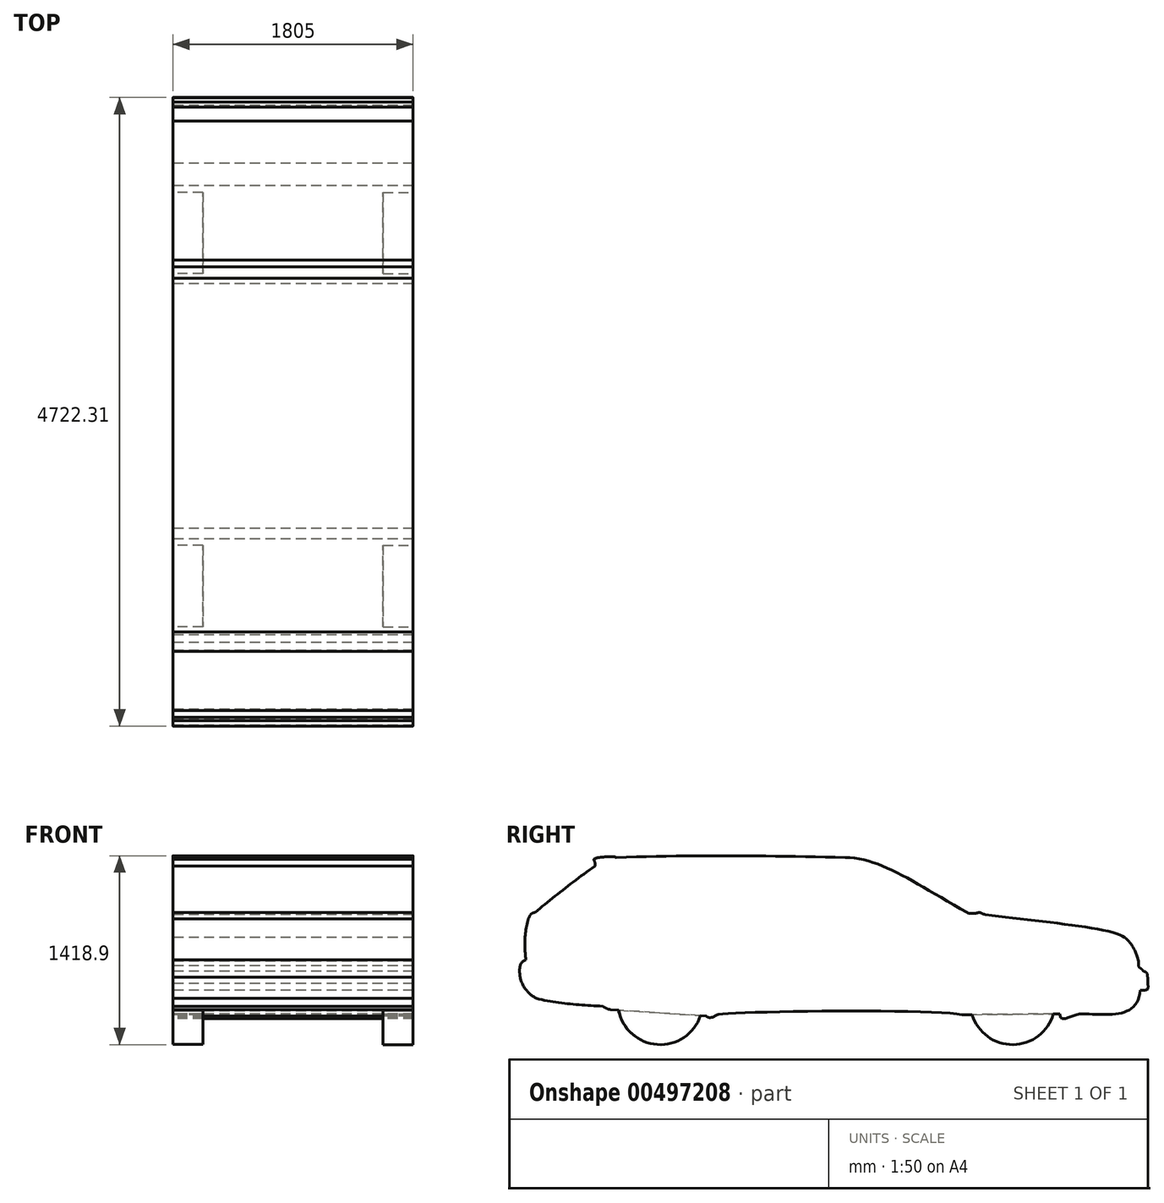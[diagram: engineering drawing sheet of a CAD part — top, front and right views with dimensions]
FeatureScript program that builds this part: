
annotation { "Feature Type Name" : "Feature", "Feature Type Description" : "" }
export const myFeature = defineFeature(function(context is Context, id is Id, definition is map)
    precondition{}
    {
        {
            var Q0;
            Q0=qCreatedBy(makeId("Right.planeOp"),FACE);
            var sketch = newSketch(context, id + "F0", { "sketchPlane" : qUnion([Q0])});
            skFitSpline(sketch, "E0", {"points": [v(1014.45, 1014.59) * mm, v(98.52, 1428.8) * mm], "startDerivative": vector(-1208.9, 676.68) * mm, "endDerivative": vector(-805.93, 15.2) * mm});
            skFitSpline(sketch, "E1", {"points": [v(98.52, 1428.8) * mm, v(-1621.84, 1428.8) * mm], "startDerivative": vector(-1726.02, 42.39) * mm, "endDerivative": vector(-1726.24, -56.33) * mm});
            skFitSpline(sketch, "E2", {"points": [v(-1621.84, 1428.8) * mm, v(-1641.32, 1434.74) * mm], "startDerivative": vector(-28.04, -1.19) * mm, "endDerivative": vector(-37.07, 0.95) * mm});
            skFitSpline(sketch, "E3", {"points": [v(-1641.32, 1434.74) * mm, v(-1789.27, 1416.05) * mm], "startDerivative": vector(-186.28, 7.6) * mm, "endDerivative": vector(-4.75, -28.51) * mm});
            skFitSpline(sketch, "E4", {"points": [v(-1789.27, 1416.05) * mm, v(-1782.87, 1389.44) * mm], "startDerivative": vector(-3.8, -40.87) * mm, "endDerivative": vector(7.6, -42.77) * mm});
            skFitSpline(sketch, "E5", {"points": [v(-1782.87, 1389.44) * mm, v(-1782.87, 1364.14) * mm], "startDerivative": vector(4.26, -24.24) * mm, "endDerivative": vector(-10.86, -12.24) * mm});
            skFitSpline(sketch, "E6", {"points": [v(-1782.87, 1364.14) * mm, v(-2232.94, 1015.64) * mm], "startDerivative": vector(-478.61, -337.99) * mm, "endDerivative": vector(-426.28, -348.1) * mm});
            skFitSpline(sketch, "E7", {"points": [v(-2232.94, 1015.64) * mm, v(-2282.57, 967.54) * mm], "startDerivative": vector(-103.2, -19.3) * mm, "endDerivative": vector(-40.32, -90.05) * mm});
            skFitSpline(sketch, "E8", {"points": [v(-2282.57, 967.54) * mm, v(-2301.84, 658.4) * mm], "startDerivative": vector(-98.12, -310.48) * mm, "endDerivative": vector(29.57, -294.35) * mm});
            skFitSpline(sketch, "E9", {"points": [v(-2301.84, 658.4) * mm, v(-2344.4, 529.38) * mm], "startDerivative": vector(-163.97, -44.35) * mm, "endDerivative": vector(22.85, -147.85) * mm});
            skFitSpline(sketch, "E10", {"points": [v(-2344.4, 529.38) * mm, v(-2222.54, 368.99) * mm], "startDerivative": vector(49.73, -247.3) * mm, "endDerivative": vector(158.6, -94.08) * mm});
            skFitSpline(sketch, "E11", {"points": [v(-2222.54, 368.99) * mm, v(-1723, 310.74) * mm], "startDerivative": vector(462.35, -111.56) * mm, "endDerivative": vector(508.05, -28.23) * mm});
            skFitSpline(sketch, "E12", {"points": [v(-1723, 310.74) * mm, v(-1637.88, 306.71) * mm], "startDerivative": vector(77.96, -63.17) * mm, "endDerivative": vector(4.03, 115.59) * mm});
            skFitSpline(sketch, "E13", {"points": [v(-1637.88, 306.71) * mm, v(-1412.97, 702.76) * mm], "startDerivative": vector(-33.6, 659.93) * mm, "endDerivative": vector(388.43, 166.66) * mm});
            skFitSpline(sketch, "E14", {"points": [v(-1412.97, 702.76) * mm, v(-989.15, 553.57) * mm], "startDerivative": vector(462.35, 104.84) * mm, "endDerivative": vector(279.56, -498.64) * mm});
            skFitSpline(sketch, "E15", {"points": [v(-989.15, 553.57) * mm, v(-944.22, 237) * mm], "startDerivative": vector(157.63, -296.38) * mm, "endDerivative": vector(-8.06, -315.85) * mm});
            skFitSpline(sketch, "E16", {"points": [v(-944.22, 237) * mm, v(-865.37, 246.45) * mm], "startDerivative": vector(2.69, -26.88) * mm, "endDerivative": vector(133.06, 102.15) * mm});
            skFitSpline(sketch, "E17", {"points": [v(-865.37, 246.45) * mm, v(973.8, 246.45) * mm], "startDerivative": vector(92.89, 73.19) * mm, "endDerivative": vector(693.53, -148.45) * mm});
            skFitSpline(sketch, "E18", {"points": [v(973.8, 246.45) * mm, v(1331.5, 736.23) * mm], "startDerivative": vector(26.53, 662.38) * mm, "endDerivative": vector(897.39, 74.6) * mm});
            skFitSpline(sketch, "E19", {"points": [v(1331.5, 736.23) * mm, v(1709.74, 254) * mm], "startDerivative": vector(691.69, 18.08) * mm, "endDerivative": vector(-90.42, -870.26) * mm});
            skFitSpline(sketch, "E20", {"points": [v(1709.74, 254) * mm, v(1880.03, 254) * mm], "startDerivative": vector(15.82, -241.86) * mm, "endDerivative": vector(259.95, 13.56) * mm});
            skFitSpline(sketch, "E21", {"points": [v(1880.03, 254) * mm, v(2315.53, 431.07) * mm], "startDerivative": vector(580.93, -15.82) * mm, "endDerivative": vector(63.3, 660.04) * mm});
            skFitSpline(sketch, "E22", {"points": [v(2315.53, 431.07) * mm, v(2372.04, 482.3) * mm], "startDerivative": vector(180.83, 0) * mm, "endDerivative": vector(-11.3, 153.7) * mm});
            skFitSpline(sketch, "E23", {"points": [v(2372.04, 482.3) * mm, v(2338.14, 574.99) * mm], "startDerivative": vector(-13.56, 223.78) * mm, "endDerivative": vector(-115.28, 36.17) * mm});
            skFitSpline(sketch, "E24", {"points": [v(2338.14, 574.99) * mm, v(2301.22, 614.92) * mm], "startDerivative": vector(-38.43, 70.07) * mm, "endDerivative": vector(-40.69, 83.64) * mm});
            skFitSpline(sketch, "E25", {"points": [v(2301.22, 614.92) * mm, v(2301.22, 649.58) * mm], "startDerivative": vector(0, 34.66) * mm, "endDerivative": vector(0, 34.66) * mm});
            skFitSpline(sketch, "E26", {"points": [v(2301.22, 649.58) * mm, v(2198, 827.4) * mm], "startDerivative": vector(-72.33, 250.9) * mm, "endDerivative": vector(-169.53, 144.67) * mm});
            skFitSpline(sketch, "E27", {"points": [v(2198, 827.4) * mm, v(1151.42, 999.95) * mm], "startDerivative": vector(-291.6, 235.08) * mm, "endDerivative": vector(-1082.74, 153.7) * mm});
            skFitSpline(sketch, "E28", {"points": [v(1151.42, 999.95) * mm, v(1101.48, 1014.96) * mm], "startDerivative": vector(-72.96, 5.5) * mm, "endDerivative": vector(-65.55, 0) * mm});
            skFitSpline(sketch, "E29", {"points": [v(1101.48, 1014.96) * mm, v(1014.45, 1014.59) * mm], "startDerivative": vector(-97.2, -27.13) * mm, "endDerivative": vector(-49.59, 34.86) * mm});
            skLineSegment(sketch, "E30", {"start": v(1709.74, 254) * mm, "end": v(973.8, 246.45) * mm});
            skLineSegment(sketch, "E31", {"start": v(-944.22, 237) * mm, "end": v(-1663.57, 285.48) * mm});
            skSolve(sketch);
        }
        {
            var Q0;
            Q0=makeQuery(id+"F0.imprint","IMPRINT",FACE,{"disambiguationData":[TD([[makeQuery(id+"F0.imprint","IMPRINT",EDGE,{"derivedFrom":sQuery(id+"F0.wireOp",EDGE,"E0")}),1.0]])]});
            var Q1;
            Q1=makeQuery(id+"F0.imprint","IMPRINT",FACE,{"disambiguationData":[TD([[makeQuery(id+"F0.imprint","IMPRINT",EDGE,{"derivedFrom":sQuery(id+"F0.wireOp",EDGE,"E18")}),-1.0]])]});
            var Q2;
            {var subQ0=sQuery(id+"F0.wireOp",EDGE,"E13");Q2=makeQuery(id+"F0.imprint","IMPRINT",FACE,{"disambiguationData":[TD([[makeQuery(id+"F0.imprint","IMPRINT",EDGE,{"derivedFrom":subQ0}),-1.0]])]});}
            extrude(context, id + "F1", {"entities" : qUnion([Q0, Q1, Q2]), "endBound" : BoundingType.SYMMETRIC, "depth" : 1805 * mm});
        }
        {
            var Q0;
            Q0=makeQuery(id+"F1.opExtrude","CAP_FACE",FACE,{"disambiguationData":[OSD([sQuery(id+"F0.wireOp",EDGE,"E0"),sQuery(id+"F0.wireOp",EDGE,"E1"),sQuery(id+"F0.wireOp",EDGE,"E2"),sQuery(id+"F0.wireOp",EDGE,"E3"),sQuery(id+"F0.wireOp",EDGE,"E4"),sQuery(id+"F0.wireOp",EDGE,"E5"),sQuery(id+"F0.wireOp",EDGE,"E6"),sQuery(id+"F0.wireOp",EDGE,"E7"),sQuery(id+"F0.wireOp",EDGE,"E8"),sQuery(id+"F0.wireOp",EDGE,"E9"),sQuery(id+"F0.wireOp",EDGE,"E10"),sQuery(id+"F0.wireOp",EDGE,"E11"),sQuery(id+"F0.wireOp",EDGE,"E12"),sQuery(id+"F0.wireOp",EDGE,"E16"),sQuery(id+"F0.wireOp",EDGE,"E17"),sQuery(id+"F0.wireOp",EDGE,"E20"),sQuery(id+"F0.wireOp",EDGE,"E21"),sQuery(id+"F0.wireOp",EDGE,"E22"),sQuery(id+"F0.wireOp",EDGE,"E23"),sQuery(id+"F0.wireOp",EDGE,"E24"),sQuery(id+"F0.wireOp",EDGE,"E25"),sQuery(id+"F0.wireOp",EDGE,"E26"),sQuery(id+"F0.wireOp",EDGE,"E27"),sQuery(id+"F0.wireOp",EDGE,"E28"),sQuery(id+"F0.wireOp",EDGE,"E29"),sQuery(id+"F0.wireOp",EDGE,"E30"),sQuery(id+"F0.wireOp",EDGE,"E31")])],"isStart":true});
            var sketch = newSketch(context, id + "F2", { "sketchPlane" : qUnion([Q0])});
            skCircle(sketch, "E32", {"center": v(-1355.52, 340.73) * mm, "radius": 318 * mm});
            skCircle(sketch, "E33", {"center": v(1292.57, 340.73) * mm, "radius": 318 * mm});
            skSolve(sketch);
        }
        {
            var Q0;
            {var subQ0=sQuery(id+"F2.wireOp",EDGE,"E32");var subQ1=makeQuery(id+"F1.opExtrude","CAP_EDGE",EDGE,{"disambiguationData":[OSD([sQuery(id+"F0.wireOp",EDGE,"E30")])],"isStart":true});var subQ2=makeQuery(id+"F2.imprint","INTERSECT",VERTEX,{"disambiguationData":[OD(0.0)],"derivedFrom":[subQ1,subQ0]});Q0=makeQuery(id+"F2.imprint","IMPRINT",FACE,{"disambiguationData":[TD([[makeQuery(id+"F2.imprint","IMPRINT",EDGE,{"disambiguationData":[TD([[subQ2,-1.0]])],"derivedFrom":subQ0}),1.0]])]});}
            var Q1;
            {var subQ0=sQuery(id+"F2.wireOp",EDGE,"E32");var subQ1=makeQuery(id+"F1.opExtrude","CAP_EDGE",EDGE,{"disambiguationData":[OSD([sQuery(id+"F0.wireOp",EDGE,"E30")])],"isStart":true});var subQ2=makeQuery(id+"F2.imprint","INTERSECT",VERTEX,{"disambiguationData":[OD(0.0)],"derivedFrom":[subQ1,subQ0]});Q1=makeQuery(id+"F2.imprint","IMPRINT",FACE,{"disambiguationData":[TD([[makeQuery(id+"F2.imprint","IMPRINT",EDGE,{"disambiguationData":[TD([[subQ2,1.0]])],"derivedFrom":subQ0}),1.0]])]});}
            var Q2;
            {var subQ0=sQuery(id+"F2.wireOp",EDGE,"E33");var subQ1=makeQuery(id+"F1.opExtrude","CAP_EDGE",EDGE,{"disambiguationData":[OSD([sQuery(id+"F0.wireOp",EDGE,"E31")])],"isStart":true});var subQ2=makeQuery(id+"F2.imprint","INTERSECT",VERTEX,{"disambiguationData":[OD(0.0)],"derivedFrom":[subQ1,subQ0]});Q2=makeQuery(id+"F2.imprint","IMPRINT",FACE,{"disambiguationData":[TD([[makeQuery(id+"F2.imprint","IMPRINT",EDGE,{"disambiguationData":[TD([[subQ2,-1.0]])],"derivedFrom":subQ0}),1.0]])]});}
            var Q3;
            {var subQ0=sQuery(id+"F2.wireOp",EDGE,"E33");var subQ1=makeQuery(id+"F1.opExtrude","CAP_EDGE",EDGE,{"disambiguationData":[OSD([sQuery(id+"F0.wireOp",EDGE,"E31")])],"isStart":true});var subQ2=makeQuery(id+"F2.imprint","INTERSECT",VERTEX,{"disambiguationData":[OD(0.0)],"derivedFrom":[subQ1,subQ0]});Q3=makeQuery(id+"F2.imprint","IMPRINT",FACE,{"disambiguationData":[TD([[makeQuery(id+"F2.imprint","IMPRINT",EDGE,{"disambiguationData":[TD([[subQ2,1.0]])],"derivedFrom":subQ0}),1.0]])]});}
            extrude(context, id + "F3", {"entities" : qUnion([Q0, Q1, Q2, Q3]), "operationType" : NewBodyOperationType.ADD, "oppositeDirection" : true, "depth" : 225 * mm});
        }
        {
            var Q0;
            Q0=makeQuery(id+"F1.opExtrude","CAP_FACE",FACE,{"disambiguationData":[OSD([sQuery(id+"F0.wireOp",EDGE,"E0"),sQuery(id+"F0.wireOp",EDGE,"E1"),sQuery(id+"F0.wireOp",EDGE,"E2"),sQuery(id+"F0.wireOp",EDGE,"E3"),sQuery(id+"F0.wireOp",EDGE,"E4"),sQuery(id+"F0.wireOp",EDGE,"E5"),sQuery(id+"F0.wireOp",EDGE,"E6"),sQuery(id+"F0.wireOp",EDGE,"E7"),sQuery(id+"F0.wireOp",EDGE,"E8"),sQuery(id+"F0.wireOp",EDGE,"E9"),sQuery(id+"F0.wireOp",EDGE,"E10"),sQuery(id+"F0.wireOp",EDGE,"E11"),sQuery(id+"F0.wireOp",EDGE,"E12"),sQuery(id+"F0.wireOp",EDGE,"E16"),sQuery(id+"F0.wireOp",EDGE,"E17"),sQuery(id+"F0.wireOp",EDGE,"E20"),sQuery(id+"F0.wireOp",EDGE,"E21"),sQuery(id+"F0.wireOp",EDGE,"E22"),sQuery(id+"F0.wireOp",EDGE,"E23"),sQuery(id+"F0.wireOp",EDGE,"E24"),sQuery(id+"F0.wireOp",EDGE,"E25"),sQuery(id+"F0.wireOp",EDGE,"E26"),sQuery(id+"F0.wireOp",EDGE,"E27"),sQuery(id+"F0.wireOp",EDGE,"E28"),sQuery(id+"F0.wireOp",EDGE,"E29"),sQuery(id+"F0.wireOp",EDGE,"E30"),sQuery(id+"F0.wireOp",EDGE,"E31")])],"isStart":false});
            var sketch = newSketch(context, id + "F4", { "sketchPlane" : qUnion([Q0])});
            skCircle(sketch, "E34", {"center": v(-1292.02, 340.3) * mm, "radius": 318 * mm});
            skCircle(sketch, "E35", {"center": v(1355.59, 340.3) * mm, "radius": 318 * mm});
            skSolve(sketch);
        }
        {
            var Q0;
            {var subQ0=sQuery(id+"F4.wireOp",EDGE,"E34");var subQ1=makeQuery(id+"F1.opExtrude","CAP_EDGE",EDGE,{"disambiguationData":[OSD([sQuery(id+"F0.wireOp",EDGE,"E31")])],"isStart":false});var subQ2=makeQuery(id+"F4.imprint","INTERSECT",VERTEX,{"disambiguationData":[OD(0.0)],"derivedFrom":[subQ1,subQ0]});Q0=makeQuery(id+"F4.imprint","IMPRINT",FACE,{"disambiguationData":[TD([[makeQuery(id+"F4.imprint","IMPRINT",EDGE,{"disambiguationData":[TD([[subQ2,-1.0]])],"derivedFrom":subQ0}),1.0]])]});}
            var Q1;
            {var subQ0=sQuery(id+"F4.wireOp",EDGE,"E34");var subQ1=makeQuery(id+"F1.opExtrude","CAP_EDGE",EDGE,{"disambiguationData":[OSD([sQuery(id+"F0.wireOp",EDGE,"E31")])],"isStart":false});var subQ2=makeQuery(id+"F4.imprint","INTERSECT",VERTEX,{"disambiguationData":[OD(0.0)],"derivedFrom":[subQ1,subQ0]});Q1=makeQuery(id+"F4.imprint","IMPRINT",FACE,{"disambiguationData":[TD([[makeQuery(id+"F4.imprint","IMPRINT",EDGE,{"disambiguationData":[TD([[subQ2,1.0]])],"derivedFrom":subQ0}),1.0]])]});}
            var Q2;
            {var subQ0=sQuery(id+"F4.wireOp",EDGE,"E35");var subQ1=makeQuery(id+"F1.opExtrude","CAP_EDGE",EDGE,{"disambiguationData":[OSD([sQuery(id+"F0.wireOp",EDGE,"E30")])],"isStart":false});var subQ2=makeQuery(id+"F4.imprint","INTERSECT",VERTEX,{"disambiguationData":[OD(0.0)],"derivedFrom":[subQ1,subQ0]});Q2=makeQuery(id+"F4.imprint","IMPRINT",FACE,{"disambiguationData":[TD([[makeQuery(id+"F4.imprint","IMPRINT",EDGE,{"disambiguationData":[TD([[subQ2,-1.0]])],"derivedFrom":subQ0}),1.0]])]});}
            var Q3;
            {var subQ0=sQuery(id+"F4.wireOp",EDGE,"E35");var subQ1=makeQuery(id+"F1.opExtrude","CAP_EDGE",EDGE,{"disambiguationData":[OSD([sQuery(id+"F0.wireOp",EDGE,"E30")])],"isStart":false});var subQ2=makeQuery(id+"F4.imprint","INTERSECT",VERTEX,{"disambiguationData":[OD(0.0)],"derivedFrom":[subQ1,subQ0]});Q3=makeQuery(id+"F4.imprint","IMPRINT",FACE,{"disambiguationData":[TD([[makeQuery(id+"F4.imprint","IMPRINT",EDGE,{"disambiguationData":[TD([[subQ2,1.0]])],"derivedFrom":subQ0}),1.0]])]});}
            extrude(context, id + "F5", {"entities" : qUnion([Q0, Q1, Q2, Q3]), "operationType" : NewBodyOperationType.ADD, "oppositeDirection" : true, "depth" : 225 * mm});
        }
    });
